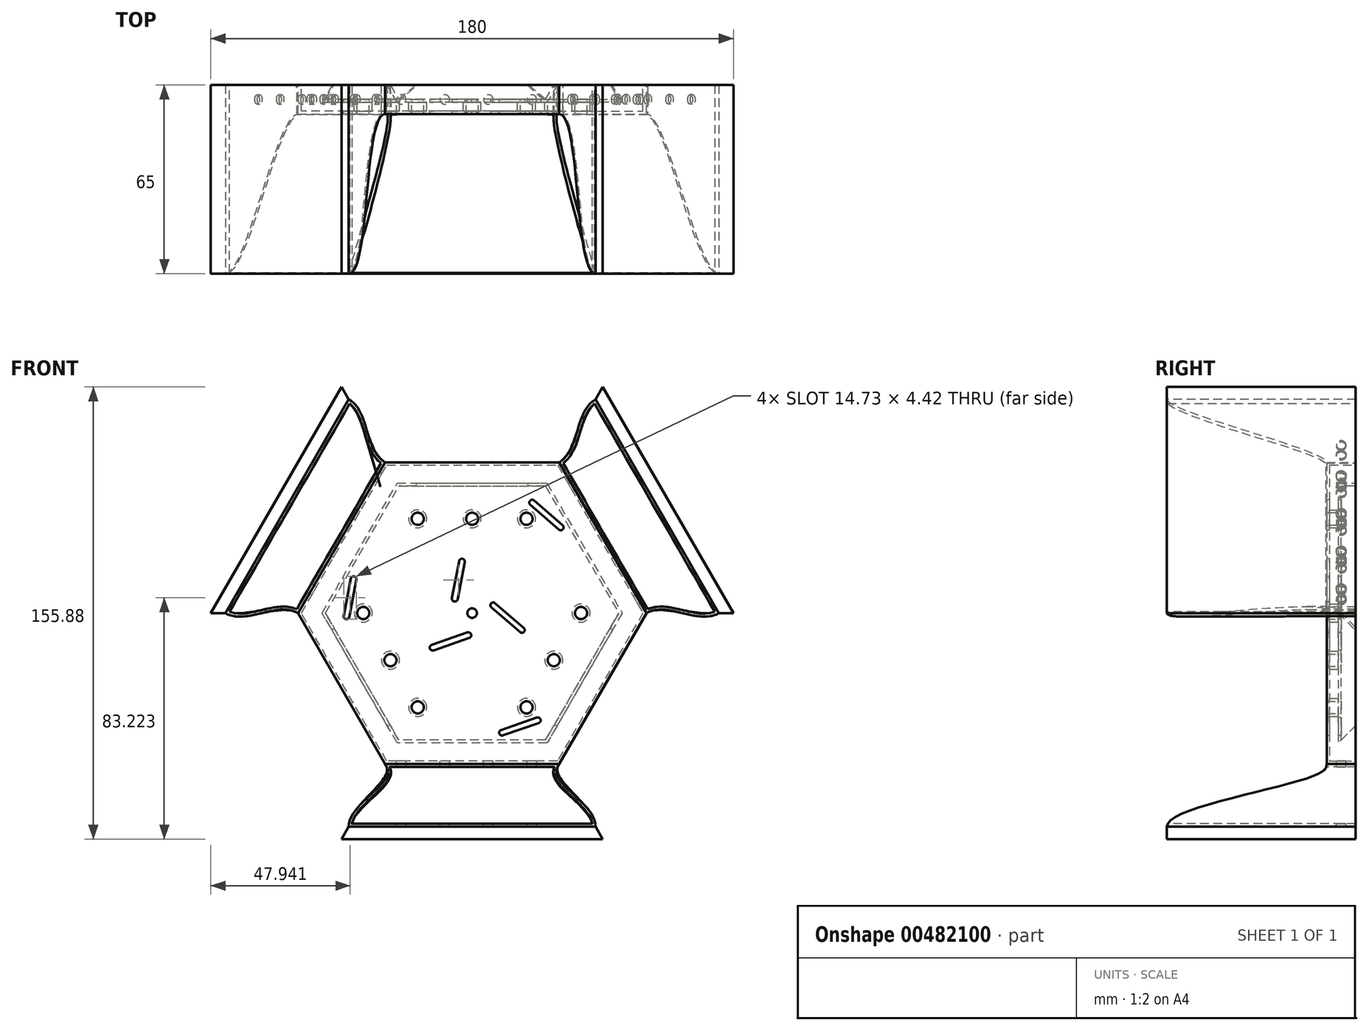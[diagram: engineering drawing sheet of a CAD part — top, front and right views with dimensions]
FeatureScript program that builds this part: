
annotation { "Feature Type Name" : "Feature", "Feature Type Description" : "" }
export const myFeature = defineFeature(function(context is Context, id is Id, definition is map)
    precondition{}
    {
        {
            var Q0;
            Q0=qCreatedBy(makeId("Front.planeOp"),FACE);
            var sketch = newSketch(context, id + "F0", { "sketchPlane" : qUnion([Q0])});
            skCircle(sketch, "E0.cCircle", {"center": v(0, 0) * mm, "radius": 60 * mm, "construction": true});
            skLineSegment(sketch, "E0.0", {"start": v(30, 51.96) * mm, "end": v(60, 0) * mm});
            skLineSegment(sketch, "E0.1", {"start": v(60, 0) * mm, "end": v(30, -51.96) * mm});
            skLineSegment(sketch, "E0.2", {"start": v(30, -51.96) * mm, "end": v(-30, -51.96) * mm});
            skLineSegment(sketch, "E0.3", {"start": v(-30, -51.96) * mm, "end": v(-60, 0) * mm});
            skLineSegment(sketch, "E0.4", {"start": v(-60, 0) * mm, "end": v(-30, 51.96) * mm});
            skLineSegment(sketch, "E0.5", {"start": v(-30, 51.96) * mm, "end": v(30, 51.96) * mm});
            skSolve(sketch);
        }
        {
            var Q0;
            Q0 = qSketchRegion(id + "F0", true);
            var Q1;
            Q1=makeQuery(id+"F0.imprint","IMPRINT",FACE,{"disambiguationData":[TD([[makeQuery(id+"F0.imprint","IMPRINT",EDGE,{"derivedFrom":sQuery(id+"F0.wireOp",EDGE,"E0.0")}),-1.0]])]});
            extrude(context, id + "F1", {"entities" : qUnion([Q0, Q1]), "endBound" : BoundingType.SYMMETRIC, "depth" : 10 * mm});
        }
        {
            var Q0;
            Q0=qCreatedBy(makeId("Front.planeOp"),FACE);
            var sketch = newSketch(context, id + "F2", { "sketchPlane" : qUnion([Q0])});
            skCircle(sketch, "E1.cCircle", {"center": v(0, 0) * mm, "radius": 50.5 * mm, "construction": true});
            skLineSegment(sketch, "E1.0", {"start": v(25.25, -43.73) * mm, "end": v(-25.25, -43.73) * mm});
            skLineSegment(sketch, "E1.1", {"start": v(-25.25, -43.73) * mm, "end": v(-50.5, 0) * mm});
            skLineSegment(sketch, "E1.2", {"start": v(-50.5, 0) * mm, "end": v(-25.25, 43.73) * mm});
            skLineSegment(sketch, "E1.3", {"start": v(-25.25, 43.73) * mm, "end": v(25.25, 43.73) * mm});
            skLineSegment(sketch, "E1.4", {"start": v(25.25, 43.73) * mm, "end": v(50.5, 0) * mm});
            skLineSegment(sketch, "E1.5", {"start": v(50.5, 0) * mm, "end": v(25.25, -43.73) * mm});
            skSolve(sketch);
        }
        {
            var Q0;
            Q0 = qSketchRegion(id + "F2", true);
            extrude(context, id + "F3", {"entities" : qUnion([Q0]), "oppositeDirection" : true, "depth" : 15 * mm});
        }
        {
            var Q0;
            Q0=makeQuery(id+"F3.opExtrude","SWEPT_BODY",BODY,{"disambiguationData":[OSD([sQuery(id+"F2.wireOp",EDGE,"E1.0"),sQuery(id+"F2.wireOp",EDGE,"E1.1"),sQuery(id+"F2.wireOp",EDGE,"E1.2"),sQuery(id+"F2.wireOp",EDGE,"E1.3"),sQuery(id+"F2.wireOp",EDGE,"E1.4"),sQuery(id+"F2.wireOp",EDGE,"E1.5")])]});
            var Q1;
            Q1=makeQuery(id+"F1.opExtrude","SWEPT_BODY",BODY,{"disambiguationData":[OSD([sQuery(id+"F0.wireOp",EDGE,"E0.0"),sQuery(id+"F0.wireOp",EDGE,"E0.1"),sQuery(id+"F0.wireOp",EDGE,"E0.2"),sQuery(id+"F0.wireOp",EDGE,"E0.3"),sQuery(id+"F0.wireOp",EDGE,"E0.4"),sQuery(id+"F0.wireOp",EDGE,"E0.5")])]});
            booleanBodies(context, id + "F4", {"operationType" : BooleanOperationType.SUBTRACTION, "tools" : qUnion([Q0]), "targets" : qUnion([Q1])});
        }
        {
            var Q0;
            Q0=qCreatedBy(makeId("Front.planeOp"),FACE);
            var sketch = newSketch(context, id + "F5", { "sketchPlane" : qUnion([Q0])});
            skCircle(sketch, "E2.cCircle", {"center": v(0, 0) * mm, "radius": 37.5 * mm, "construction": true});
            skLineSegment(sketch, "E2.0", {"start": v(-18.75, 32.48) * mm, "end": v(18.75, 32.48) * mm});
            skLineSegment(sketch, "E2.1", {"start": v(18.75, 32.48) * mm, "end": v(37.5, 0) * mm});
            skLineSegment(sketch, "E2.2", {"start": v(37.5, 0) * mm, "end": v(18.75, -32.48) * mm});
            skLineSegment(sketch, "E2.3", {"start": v(18.75, -32.48) * mm, "end": v(-18.75, -32.48) * mm});
            skLineSegment(sketch, "E2.4", {"start": v(-18.75, -32.48) * mm, "end": v(-37.5, 0) * mm});
            skLineSegment(sketch, "E2.5", {"start": v(-37.5, 0) * mm, "end": v(-18.75, 32.48) * mm});
            skPoint(sketch, "E3", {"position": v(18.75, 32.48) * mm});
            skPoint(sketch, "E4", {"position": v(0, 32.48) * mm});
            skPoint(sketch, "E5", {"position": v(-18.75, 32.48) * mm});
            skPoint(sketch, "E6", {"position": v(-37.5, 0) * mm});
            skPoint(sketch, "E7", {"position": v(-18.75, -32.48) * mm});
            skPoint(sketch, "E8", {"position": v(-28.13, -16.24) * mm});
            skPoint(sketch, "E9", {"position": v(18.75, -32.48) * mm});
            skPoint(sketch, "E10", {"position": v(37.5, 0) * mm});
            skPoint(sketch, "E11", {"position": v(28.13, -16.24) * mm});
            skSolve(sketch);
        }
        {
            var Q0;
            Q0=sQuery(id+"F5.wireOp",VERTEX,"E3");
            var Q1;
            Q1=sQuery(id+"F5.wireOp",VERTEX,"E4");
            var Q2;
            Q2=sQuery(id+"F5.wireOp",VERTEX,"E5");
            var Q3;
            Q3=sQuery(id+"F5.wireOp",VERTEX,"E6");
            var Q4;
            Q4=sQuery(id+"F5.wireOp",VERTEX,"E8");
            var Q5;
            Q5=sQuery(id+"F5.wireOp",VERTEX,"E7");
            var Q6;
            Q6=sQuery(id+"F5.wireOp",VERTEX,"E9");
            var Q7;
            Q7=sQuery(id+"F5.wireOp",VERTEX,"E11");
            var Q8;
            Q8=sQuery(id+"F5.wireOp",VERTEX,"E10");
            var Q9;
            Q9=makeQuery(id+"F1.opExtrude","SWEPT_BODY",BODY,{"disambiguationData":[OSD([sQuery(id+"F0.wireOp",EDGE,"E0.0"),sQuery(id+"F0.wireOp",EDGE,"E0.1"),sQuery(id+"F0.wireOp",EDGE,"E0.2"),sQuery(id+"F0.wireOp",EDGE,"E0.3"),sQuery(id+"F0.wireOp",EDGE,"E0.4"),sQuery(id+"F0.wireOp",EDGE,"E0.5")])]});
            hole(context, id + "F6", {"style" : HoleStyle.SIMPLE, "endStyle" : HoleEndStyle.BLIND, "oppositeDirection" : true, "holeDiameter" : 4.2 * mm, "holeDepth" : 8 * mm, "isTappedThrough" : true, "tappedDepth" : 12 * mm, "tapClearance" : 3, "startFromSketch" : true, "locations" : qUnion([Q0, Q1, Q2, Q3, Q4, Q5, Q6, Q7, Q8]), "scope" : qUnion([Q9])});
        }
        {
            var Q0;
            Q0=qCreatedBy(makeId("Front.planeOp"),FACE);
            cPlane(context, id + "F7", {"entities" : qUnion([Q0]), "cplaneType" : CPlaneType.OFFSET, "offset" : 60 * mm, "width" : 150 * mm, "height" : 150 * mm});
        }
        {
            var Q0;
            Q0=qCreatedBy(id+"F7.planeOp",FACE);
            var sketch = newSketch(context, id + "F8", { "sketchPlane" : qUnion([Q0])});
            skCircle(sketch, "E12.cCircle", {"center": v(0, 0) * mm, "radius": 90 * mm, "construction": true});
            skLineSegment(sketch, "E12.0", {"start": v(-90, 0) * mm, "end": v(-45, 77.94) * mm});
            skLineSegment(sketch, "E12.2", {"start": v(45, 77.94) * mm, "end": v(90, 0) * mm});
            skLineSegment(sketch, "E12.4", {"start": v(45, -77.94) * mm, "end": v(-45, -77.94) * mm});
            skPoint(sketch, "E13.cCircle.perimeterSnap0", {"position": v(-67.5, -38.97) * mm});
            skPoint(sketch, "E13.0.startSnap0", {"position": v(-67.5, -38.97) * mm});
            skCircle(sketch, "E14.cCircle", {"center": v(0, 0) * mm, "radius": 85 * mm, "construction": true});
            skLineSegment(sketch, "E14.1", {"start": v(42.5, -73.61) * mm, "end": v(-42.5, -73.61) * mm});
            skLineSegment(sketch, "E14.3", {"start": v(-85, 0) * mm, "end": v(-42.5, 73.61) * mm});
            skLineSegment(sketch, "E14.5", {"start": v(42.5, 73.61) * mm, "end": v(85, 0) * mm});
            skLineSegment(sketch, "E15", {"start": v(-42.5, 73.61) * mm, "end": v(-45, 77.94) * mm});
            skLineSegment(sketch, "E16", {"start": v(-85, 0) * mm, "end": v(-90, 0) * mm});
            skLineSegment(sketch, "E17", {"start": v(42.5, 73.61) * mm, "end": v(45, 77.94) * mm});
            skLineSegment(sketch, "E18", {"start": v(85, 0) * mm, "end": v(90, 0) * mm});
            skLineSegment(sketch, "E19", {"start": v(42.5, -73.61) * mm, "end": v(45, -77.94) * mm});
            skLineSegment(sketch, "E20", {"start": v(-45, -77.94) * mm, "end": v(-42.5, -73.61) * mm});
            skSolve(sketch);
        }
        {
            var Q0;
            Q0 = qSketchRegion(id + "F8", true);
            var Q1;
            Q1=makeQuery(id+"F8.imprint","IMPRINT",FACE,{"disambiguationData":[TD([[makeQuery(id+"F8.imprint","IMPRINT",EDGE,{"derivedFrom":sQuery(id+"F8.wireOp",EDGE,"E12.0")}),-1.0]])]});
            var Q2;
            Q2=makeQuery(id+"F1.opExtrude","CAP_FACE",FACE,{"disambiguationData":[OSD([sQuery(id+"F0.wireOp",EDGE,"E0.0"),sQuery(id+"F0.wireOp",EDGE,"E0.1"),sQuery(id+"F0.wireOp",EDGE,"E0.2"),sQuery(id+"F0.wireOp",EDGE,"E0.3"),sQuery(id+"F0.wireOp",EDGE,"E0.4"),sQuery(id+"F0.wireOp",EDGE,"E0.5")])],"isStart":true});
            extrude(context, id + "F9", {"entities" : qUnion([Q0, Q1]), "endBound" : BoundingType.UP_TO_SURFACE, "oppositeDirection" : true, "endBoundEntityFace" : qUnion([Q2]), "depth" : 60 * mm});
        }
        {
            var Q0;
            Q0=makeQuery(id+"F9.opExtrude","SWEPT_FACE",FACE,{"disambiguationData":[OSD([sQuery(id+"F8.wireOp",EDGE,"E14.3")])]});
            var Q1;
            Q1=makeQuery(id+"F1.opExtrude","SWEPT_FACE",FACE,{"disambiguationData":[OSD([sQuery(id+"F0.wireOp",EDGE,"E0.4")])]});
            loft(context, id + "F10", {"startCondition" : LoftEndDerivativeType.NORMAL_TO_PROFILE, "startMagnitude" : 1, "endCondition" : LoftEndDerivativeType.NORMAL_TO_PROFILE, "endMagnitude" : 1, "sheetProfilesArray" : [{ "sheetProfileEntities" : qUnion([Q0]) }, { "sheetProfileEntities" : qUnion([Q1]) }]});
        }
        {
            var Q0;
            Q0=makeQuery(id+"F9.opExtrude","SWEPT_FACE",FACE,{"disambiguationData":[OSD([sQuery(id+"F8.wireOp",EDGE,"E14.1")])]});
            var Q1;
            Q1=makeQuery(id+"F1.opExtrude","SWEPT_FACE",FACE,{"disambiguationData":[OSD([sQuery(id+"F0.wireOp",EDGE,"E0.2")])]});
            loft(context, id + "F11", {"startCondition" : LoftEndDerivativeType.NORMAL_TO_PROFILE, "startMagnitude" : 1, "endCondition" : LoftEndDerivativeType.MATCH_CURVATURE, "endMagnitude" : 1, "sheetProfilesArray" : [{ "sheetProfileEntities" : qUnion([Q0]) }, { "sheetProfileEntities" : qUnion([Q1]) }]});
        }
        {
            var Q0;
            Q0=makeQuery(id+"F9.opExtrude","SWEPT_FACE",FACE,{"disambiguationData":[OSD([sQuery(id+"F8.wireOp",EDGE,"E14.5")])]});
            var Q1;
            Q1=makeQuery(id+"F1.opExtrude","SWEPT_FACE",FACE,{"disambiguationData":[OSD([sQuery(id+"F0.wireOp",EDGE,"E0.0")])]});
            loft(context, id + "F12", {"startCondition" : LoftEndDerivativeType.NORMAL_TO_PROFILE, "startMagnitude" : 1, "endCondition" : LoftEndDerivativeType.NORMAL_TO_PROFILE, "endMagnitude" : 1, "sheetProfilesArray" : [{ "sheetProfileEntities" : qUnion([Q0]) }, { "sheetProfileEntities" : qUnion([Q1]) }]});
        }
        {
            var Q0;
            Q0=makeQuery(id+"F1.opExtrude","CAP_FACE",FACE,{"disambiguationData":[OSD([sQuery(id+"F0.wireOp",EDGE,"E0.0"),sQuery(id+"F0.wireOp",EDGE,"E0.1"),sQuery(id+"F0.wireOp",EDGE,"E0.2"),sQuery(id+"F0.wireOp",EDGE,"E0.3"),sQuery(id+"F0.wireOp",EDGE,"E0.4"),sQuery(id+"F0.wireOp",EDGE,"E0.5")])],"isStart":true});
            shell(context, id + "F13", {"entities" : qUnion([Q0]), "thickness" : 1 * mm});
        }
        {
            var Q0;
            Q0=makeQuery(id+"F13.opShell","OFFSET_FACE",FACE,{"disambiguationData":[OSD([sQuery(id+"F0.wireOp",EDGE,"E0.4")])]});
            cPlane(context, id + "F14", {"entities" : qUnion([Q0]), "cplaneType" : CPlaneType.OFFSET, "offset" : 0 * mm, "width" : 150 * mm, "height" : 150 * mm});
        }
        {
            var Q0;
            Q0=qCreatedBy(id+"F14.planeOp",FACE);
            var sketch = newSketch(context, id + "F15", { "sketchPlane" : qUnion([Q0])});
            skPoint(sketch, "E21", {"position": v(0, 24.42) * mm});
            skPoint(sketch, "E22.0.1.0", {"position": v(0, 9.42) * mm});
            skPoint(sketch, "E22.0.2.0", {"position": v(0, -5.58) * mm});
            skPoint(sketch, "E22.0.3.0", {"position": v(0, -20.58) * mm});
            skLineSegment(sketch, "E22.direction1", {"start": v(0, 24.42) * mm, "end": v(26.25, 24.42) * mm, "construction": true});
            skLineSegment(sketch, "E22.direction2", {"start": v(0, 24.42) * mm, "end": v(0, 9.42) * mm, "construction": true});
            skSolve(sketch);
        }
        {
            var Q0;
            Q0=makeQuery(id+"F13.opShell","OFFSET_FACE",FACE,{"disambiguationData":[OSD([sQuery(id+"F0.wireOp",EDGE,"E0.0")])]});
            var sketch = newSketch(context, id + "F16", { "sketchPlane" : qUnion([Q0])});
            skPoint(sketch, "E23", {"position": v(0, -24.42) * mm});
            skPoint(sketch, "E24.0.1.0", {"position": v(0, -9.42) * mm});
            skPoint(sketch, "E24.0.2.0", {"position": v(0, 5.58) * mm});
            skPoint(sketch, "E24.0.3.0", {"position": v(0, 20.58) * mm});
            skLineSegment(sketch, "E24.direction1", {"start": v(0, -24.42) * mm, "end": v(23.75, -24.42) * mm, "construction": true});
            skLineSegment(sketch, "E24.direction2", {"start": v(0, -24.42) * mm, "end": v(0, -9.42) * mm, "construction": true});
            skSolve(sketch);
        }
        {
            var Q0;
            Q0=makeQuery(id+"F13.opShell","OFFSET_FACE",FACE,{"disambiguationData":[OSD([sQuery(id+"F0.wireOp",EDGE,"E0.2")])]});
            var sketch = newSketch(context, id + "F17", { "sketchPlane" : qUnion([Q0])});
            skPoint(sketch, "E25", {"position": v(-24.42, 0) * mm});
            skPoint(sketch, "E26.1.0.0", {"position": v(-9.42, 0) * mm});
            skPoint(sketch, "E26.2.0.0", {"position": v(5.58, 0) * mm});
            skLineSegment(sketch, "E26.direction1", {"start": v(-24.42, 0) * mm, "end": v(-9.42, 0) * mm, "construction": true});
            skPoint(sketch, "E27.0.3.0", {"position": v(20.58, 0) * mm});
            skSolve(sketch);
        }
        {
            var Q0;
            Q0=makeQuery(id+"F13.opShell","OFFSET_EDGE",EDGE,{"disambiguationData":[OSD([sQuery(id+"F0.wireOp",EDGE,"E0.0"),sQuery(id+"F0.wireOp",EDGE,"E0.1"),sQuery(id+"F0.wireOp",EDGE,"E0.2"),sQuery(id+"F0.wireOp",EDGE,"E0.3"),sQuery(id+"F0.wireOp",EDGE,"E0.4"),sQuery(id+"F0.wireOp",EDGE,"E0.5"),sQuery(id+"F2.wireOp",EDGE,"E1.0")])]});
            chamfer(context, id + "F18", {"entities" : qUnion([Q0]), "width" : 6 * mm, "tangentPropagation" : true});
        }
        {
            var Q0;
            Q0=makeQuery(id+"F13.opShell","OFFSET_EDGE",EDGE,{"disambiguationData":[OSD([sQuery(id+"F0.wireOp",EDGE,"E0.0"),sQuery(id+"F0.wireOp",EDGE,"E0.1"),sQuery(id+"F0.wireOp",EDGE,"E0.2"),sQuery(id+"F0.wireOp",EDGE,"E0.3"),sQuery(id+"F0.wireOp",EDGE,"E0.4"),sQuery(id+"F0.wireOp",EDGE,"E0.5"),sQuery(id+"F2.wireOp",EDGE,"E1.4")])]});
            chamfer(context, id + "F19", {"entities" : qUnion([Q0]), "width" : 6 * mm, "tangentPropagation" : true});
        }
        {
            var Q0;
            Q0=makeQuery(id+"F13.opShell","OFFSET_EDGE",EDGE,{"disambiguationData":[OSD([sQuery(id+"F0.wireOp",EDGE,"E0.0"),sQuery(id+"F0.wireOp",EDGE,"E0.1"),sQuery(id+"F0.wireOp",EDGE,"E0.2"),sQuery(id+"F0.wireOp",EDGE,"E0.3"),sQuery(id+"F0.wireOp",EDGE,"E0.4"),sQuery(id+"F0.wireOp",EDGE,"E0.5"),sQuery(id+"F2.wireOp",EDGE,"E1.2")])]});
            chamfer(context, id + "F20", {"entities" : qUnion([Q0]), "width" : 6 * mm, "tangentPropagation" : true});
        }
        {
            var Q0;
            Q0=makeQuery(id+"F10.opLoft","SWEPT_FACE",FACE,{"disambiguationData":[OSD([sQuery(id+"F0.wireOp",EDGE,"E0.3"),sQuery(id+"F0.wireOp",EDGE,"E0.4"),sQuery(id+"F0.wireOp",EDGE,"E0.5"),sQuery(id+"F8.wireOp",EDGE,"E14.3"),sQuery(id+"F8.wireOp",EDGE,"E15"),sQuery(id+"F8.wireOp",EDGE,"E16")])]});
            var Q1;
            Q1=makeQuery(id+"F12.opLoft","SWEPT_FACE",FACE,{"disambiguationData":[OSD([sQuery(id+"F0.wireOp",EDGE,"E0.0"),sQuery(id+"F0.wireOp",EDGE,"E0.1"),sQuery(id+"F0.wireOp",EDGE,"E0.5"),sQuery(id+"F8.wireOp",EDGE,"E14.5"),sQuery(id+"F8.wireOp",EDGE,"E17"),sQuery(id+"F8.wireOp",EDGE,"E18")])]});
            var Q2;
            Q2=makeQuery(id+"F11.opLoft","SWEPT_FACE",FACE,{"disambiguationData":[OSD([sQuery(id+"F0.wireOp",EDGE,"E0.1"),sQuery(id+"F0.wireOp",EDGE,"E0.2"),sQuery(id+"F0.wireOp",EDGE,"E0.3"),sQuery(id+"F8.wireOp",EDGE,"E14.1"),sQuery(id+"F8.wireOp",EDGE,"E19"),sQuery(id+"F8.wireOp",EDGE,"E20")])]});
            shell(context, id + "F21", {"entities" : qUnion([Q0, Q1, Q2]), "thickness" : 1 * mm});
        }
        {
            var Q0;
            Q0=sQuery(id+"F17.wireOp",VERTEX,"E25");
            var Q1;
            Q1=sQuery(id+"F17.wireOp",VERTEX,"E26.1.0.0");
            var Q2;
            Q2=sQuery(id+"F17.wireOp",VERTEX,"E26.2.0.0");
            var Q3;
            Q3=sQuery(id+"F17.wireOp",VERTEX,"E27.0.3.0");
            var Q4;
            Q4=sQuery(id+"F16.wireOp",VERTEX,"E23");
            var Q5;
            Q5=sQuery(id+"F16.wireOp",VERTEX,"E24.0.1.0");
            var Q6;
            Q6=sQuery(id+"F16.wireOp",VERTEX,"E24.0.2.0");
            var Q7;
            Q7=sQuery(id+"F16.wireOp",VERTEX,"E24.0.3.0");
            var Q8;
            Q8=sQuery(id+"F15.wireOp",VERTEX,"E21");
            var Q9;
            Q9=sQuery(id+"F15.wireOp",VERTEX,"E22.0.1.0");
            var Q10;
            Q10=sQuery(id+"F15.wireOp",VERTEX,"E22.0.2.0");
            var Q11;
            Q11=sQuery(id+"F15.wireOp",VERTEX,"E22.0.3.0");
            var Q12;
            Q12=makeQuery(id+"F1.opExtrude","SWEPT_BODY",BODY,{"disambiguationData":[OSD([sQuery(id+"F0.wireOp",EDGE,"E0.0"),sQuery(id+"F0.wireOp",EDGE,"E0.1"),sQuery(id+"F0.wireOp",EDGE,"E0.2"),sQuery(id+"F0.wireOp",EDGE,"E0.3"),sQuery(id+"F0.wireOp",EDGE,"E0.4"),sQuery(id+"F0.wireOp",EDGE,"E0.5")])]});
            var Q13;
            Q13=makeQuery(id+"F12.opLoft","SWEPT_BODY",BODY,{"disambiguationData":[OSD([sQuery(id+"F0.wireOp",EDGE,"E0.0"),sQuery(id+"F8.wireOp",EDGE,"E14.5")])]});
            var Q14;
            Q14=makeQuery(id+"F10.opLoft","SWEPT_BODY",BODY,{"disambiguationData":[OSD([sQuery(id+"F0.wireOp",EDGE,"E0.4"),sQuery(id+"F8.wireOp",EDGE,"E14.3")])]});
            var Q15;
            Q15=makeQuery(id+"F11.opLoft","SWEPT_BODY",BODY,{"disambiguationData":[OSD([sQuery(id+"F0.wireOp",EDGE,"E0.2"),sQuery(id+"F8.wireOp",EDGE,"E14.1")])]});
            hole(context, id + "F22", {"style" : HoleStyle.SIMPLE, "endStyle" : HoleEndStyle.THROUGH, "holeDiameter" : 3.3 * mm, "isTappedThrough" : true, "tappedDepth" : 12 * mm, "tapClearance" : 3, "startFromSketch" : true, "locations" : qUnion([Q0, Q1, Q2, Q3, Q4, Q5, Q6, Q7, Q8, Q9, Q10, Q11]), "scope" : qUnion([Q12, Q13, Q14, Q15])});
        }
        {
            var Q0;
            Q0=makeQuery(id+"F1.opExtrude","CAP_FACE",FACE,{"disambiguationData":[OSD([sQuery(id+"F0.wireOp",EDGE,"E0.0"),sQuery(id+"F0.wireOp",EDGE,"E0.1"),sQuery(id+"F0.wireOp",EDGE,"E0.2"),sQuery(id+"F0.wireOp",EDGE,"E0.3"),sQuery(id+"F0.wireOp",EDGE,"E0.4"),sQuery(id+"F0.wireOp",EDGE,"E0.5")])],"isStart":false});
            var sketch = newSketch(context, id + "F23", { "sketchPlane" : qUnion([Q0])});
            skLineSegment(sketch, "E28", {"start": v(0, 32.48) * mm, "end": v(37.5, 0) * mm, "construction": true});
            skLineSegment(sketch, "E29", {"start": v(28.13, -16.24) * mm, "end": v(-18.75, -32.48) * mm, "construction": true});
            skLineSegment(sketch, "E30", {"start": v(-28.13, -16.24) * mm, "end": v(-18.75, 32.48) * mm, "construction": true});
            skLineSegment(sketch, "E31.bottom", {"start": v(-2.55, 11.2) * mm, "end": v(20.7, 38.04) * mm, "construction": true});
            skLineSegment(sketch, "E31.top", {"start": v(17.1, -5.82) * mm, "end": v(40.35, 21.02) * mm, "construction": true});
            skLineSegment(sketch, "E31.left", {"start": v(-2.55, 11.2) * mm, "end": v(7.28, 2.7) * mm, "construction": true});
            skLineSegment(sketch, "E31.right", {"start": v(20.7, 38.04) * mm, "end": v(30.52, 29.53) * mm, "construction": true});
            skLineSegment(sketch, "E32.bottom", {"start": v(-38.37, 24.43) * mm, "end": v(-3.51, 17.72) * mm, "construction": true});
            skLineSegment(sketch, "E32.top", {"start": v(-43.29, -1.1) * mm, "end": v(-8.43, -7.8) * mm, "construction": true});
            skLineSegment(sketch, "E32.left", {"start": v(-38.37, 24.43) * mm, "end": v(-40.83, 11.67) * mm, "construction": true});
            skLineSegment(sketch, "E32.right", {"start": v(-3.51, 17.72) * mm, "end": v(-5.97, 4.96) * mm, "construction": true});
            skLineSegment(sketch, "E33.bottom", {"start": v(10.98, -3.4) * mm, "end": v(22.6, -36.94) * mm, "construction": true});
            skLineSegment(sketch, "E33.top", {"start": v(-13.6, -11.9) * mm, "end": v(-1.97, -45.45) * mm, "construction": true});
            skLineSegment(sketch, "E33.left", {"start": v(10.98, -3.4) * mm, "end": v(-1.3, -7.65) * mm, "construction": true});
            skLineSegment(sketch, "E33.right", {"start": v(22.6, -36.94) * mm, "end": v(10.31, -41.2) * mm, "construction": true});
            skLineSegment(sketch, "E34", {"start": v(-5.97, 4.96) * mm, "end": v(-8.43, -7.8) * mm, "construction": true});
            skPoint(sketch, "E35", {"position": v(-40.83, 11.67) * mm});
            skLineSegment(sketch, "E36", {"start": v(-40.83, 11.67) * mm, "end": v(-43.29, -1.1) * mm, "construction": true});
            skPoint(sketch, "E37", {"position": v(-1.3, -7.65) * mm});
            skLineSegment(sketch, "E38", {"start": v(-1.3, -7.65) * mm, "end": v(-13.6, -11.9) * mm, "construction": true});
            skPoint(sketch, "E39", {"position": v(10.31, -41.2) * mm});
            skPoint(sketch, "E40", {"position": v(7.28, 2.7) * mm});
            skPoint(sketch, "E41", {"position": v(30.52, 29.53) * mm});
            skLineSegment(sketch, "E42", {"start": v(7.28, 2.7) * mm, "end": v(17.1, -5.82) * mm, "construction": true});
            skLineSegment(sketch, "E43", {"start": v(30.52, 29.53) * mm, "end": v(40.35, 21.02) * mm, "construction": true});
            skLineSegment(sketch, "E44", {"start": v(10.31, -41.2) * mm, "end": v(-1.97, -45.45) * mm, "construction": true});
            skArc(sketch, "E45.0.startCap", {"start": v(-41.81, 11.85) * mm, "mid": v(-40.64, 12.65) * mm, "end": v(-39.85, 11.48) * mm});
            skArc(sketch, "E45.0.endCap", {"start": v(-42.3, -1.29) * mm, "mid": v(-43.48, -2.08) * mm, "end": v(-44.27, -0.91) * mm});
            skLineSegment(sketch, "E45.0.left", {"start": v(-39.85, 11.48) * mm, "end": v(-42.3, -1.29) * mm});
            skLineSegment(sketch, "E45.0.right", {"start": v(-41.81, 11.85) * mm, "end": v(-44.27, -0.91) * mm});
            skArc(sketch, "E45.1.startCap", {"start": v(20.04, 37.28) * mm, "mid": v(19.94, 38.7) * mm, "end": v(21.35, 38.8) * mm});
            skArc(sketch, "E45.1.endCap", {"start": v(31.17, 30.28) * mm, "mid": v(31.27, 28.87) * mm, "end": v(29.86, 28.77) * mm});
            skLineSegment(sketch, "E45.1.left", {"start": v(21.35, 38.8) * mm, "end": v(31.17, 30.28) * mm});
            skLineSegment(sketch, "E45.1.right", {"start": v(20.04, 37.28) * mm, "end": v(29.86, 28.77) * mm});
            skArc(sketch, "E45.2.startCap", {"start": v(22.27, -36) * mm, "mid": v(23.54, -36.61) * mm, "end": v(22.92, -37.88) * mm});
            skArc(sketch, "E45.2.endCap", {"start": v(10.64, -42.14) * mm, "mid": v(9.37, -41.52) * mm, "end": v(9.98, -40.25) * mm});
            skLineSegment(sketch, "E45.2.left", {"start": v(22.92, -37.88) * mm, "end": v(10.64, -42.14) * mm});
            skLineSegment(sketch, "E45.2.right", {"start": v(22.27, -36) * mm, "end": v(9.98, -40.25) * mm});
            skArc(sketch, "E45.3.startCap", {"start": v(-1.64, -6.7) * mm, "mid": v(-0.36, -7.32) * mm, "end": v(-0.98, -8.6) * mm});
            skArc(sketch, "E45.3.endCap", {"start": v(-13.26, -12.85) * mm, "mid": v(-14.54, -12.23) * mm, "end": v(-13.92, -10.96) * mm});
            skLineSegment(sketch, "E45.3.left", {"start": v(-0.98, -8.6) * mm, "end": v(-13.26, -12.85) * mm});
            skLineSegment(sketch, "E45.3.right", {"start": v(-1.64, -6.7) * mm, "end": v(-13.92, -10.96) * mm});
            skArc(sketch, "E45.4.startCap", {"start": v(-4.5, 17.91) * mm, "mid": v(-3.32, 18.7) * mm, "end": v(-2.53, 17.53) * mm});
            skArc(sketch, "E45.4.endCap", {"start": v(-4.99, 4.77) * mm, "mid": v(-6.16, 3.98) * mm, "end": v(-6.95, 5.15) * mm});
            skLineSegment(sketch, "E45.4.left", {"start": v(-2.53, 17.53) * mm, "end": v(-4.99, 4.77) * mm});
            skLineSegment(sketch, "E45.4.right", {"start": v(-4.5, 17.91) * mm, "end": v(-6.95, 5.15) * mm});
            skArc(sketch, "E45.5.startCap", {"start": v(6.62, 1.94) * mm, "mid": v(6.52, 3.35) * mm, "end": v(7.93, 3.45) * mm});
            skArc(sketch, "E45.5.endCap", {"start": v(17.76, -5.06) * mm, "mid": v(17.86, -6.47) * mm, "end": v(16.45, -6.57) * mm});
            skLineSegment(sketch, "E45.5.left", {"start": v(7.93, 3.45) * mm, "end": v(17.76, -5.06) * mm});
            skLineSegment(sketch, "E45.5.right", {"start": v(6.62, 1.94) * mm, "end": v(16.45, -6.57) * mm});
            skSolve(sketch);
        }
        {
            var Q0;
            Q0 = qSketchRegion(id + "F23", true);
            extrude(context, id + "F24", {"entities" : qUnion([Q0]), "operationType" : NewBodyOperationType.REMOVE, "oppositeDirection" : true, "depth" : 25 * mm});
        }
        {
            var Q0;
            Q0=makeQuery(id+"F4.opBoolean","COPY",FACE,{"derivedFrom":makeQuery(id+"F3.opExtrude","CAP_FACE",FACE,{"disambiguationData":[OSD([sQuery(id+"F2.wireOp",EDGE,"E1.0"),sQuery(id+"F2.wireOp",EDGE,"E1.1"),sQuery(id+"F2.wireOp",EDGE,"E1.2"),sQuery(id+"F2.wireOp",EDGE,"E1.3"),sQuery(id+"F2.wireOp",EDGE,"E1.4"),sQuery(id+"F2.wireOp",EDGE,"E1.5")])],"isStart":true})});
            var sketch = newSketch(context, id + "F25", { "sketchPlane" : qUnion([Q0])});
            skPoint(sketch, "E46", {"position": v(0, 0) * mm});
            skSolve(sketch);
        }
        {
            var Q0;
            Q0=sQuery(id+"F25.wireOp",VERTEX,"E46");
            var Q1;
            Q1=makeQuery(id+"F1.opExtrude","SWEPT_BODY",BODY,{"disambiguationData":[OSD([sQuery(id+"F0.wireOp",EDGE,"E0.0"),sQuery(id+"F0.wireOp",EDGE,"E0.1"),sQuery(id+"F0.wireOp",EDGE,"E0.2"),sQuery(id+"F0.wireOp",EDGE,"E0.3"),sQuery(id+"F0.wireOp",EDGE,"E0.4"),sQuery(id+"F0.wireOp",EDGE,"E0.5")])]});
            hole(context, id + "F26", {"style" : HoleStyle.SIMPLE, "endStyle" : HoleEndStyle.BLIND, "holeDiameter" : 3.3 * mm, "holeDepth" : 8 * mm, "isTappedThrough" : true, "tappedDepth" : 12 * mm, "tapClearance" : 3, "startFromSketch" : true, "locations" : qUnion([Q0]), "scope" : qUnion([Q1])});
        }
    });
